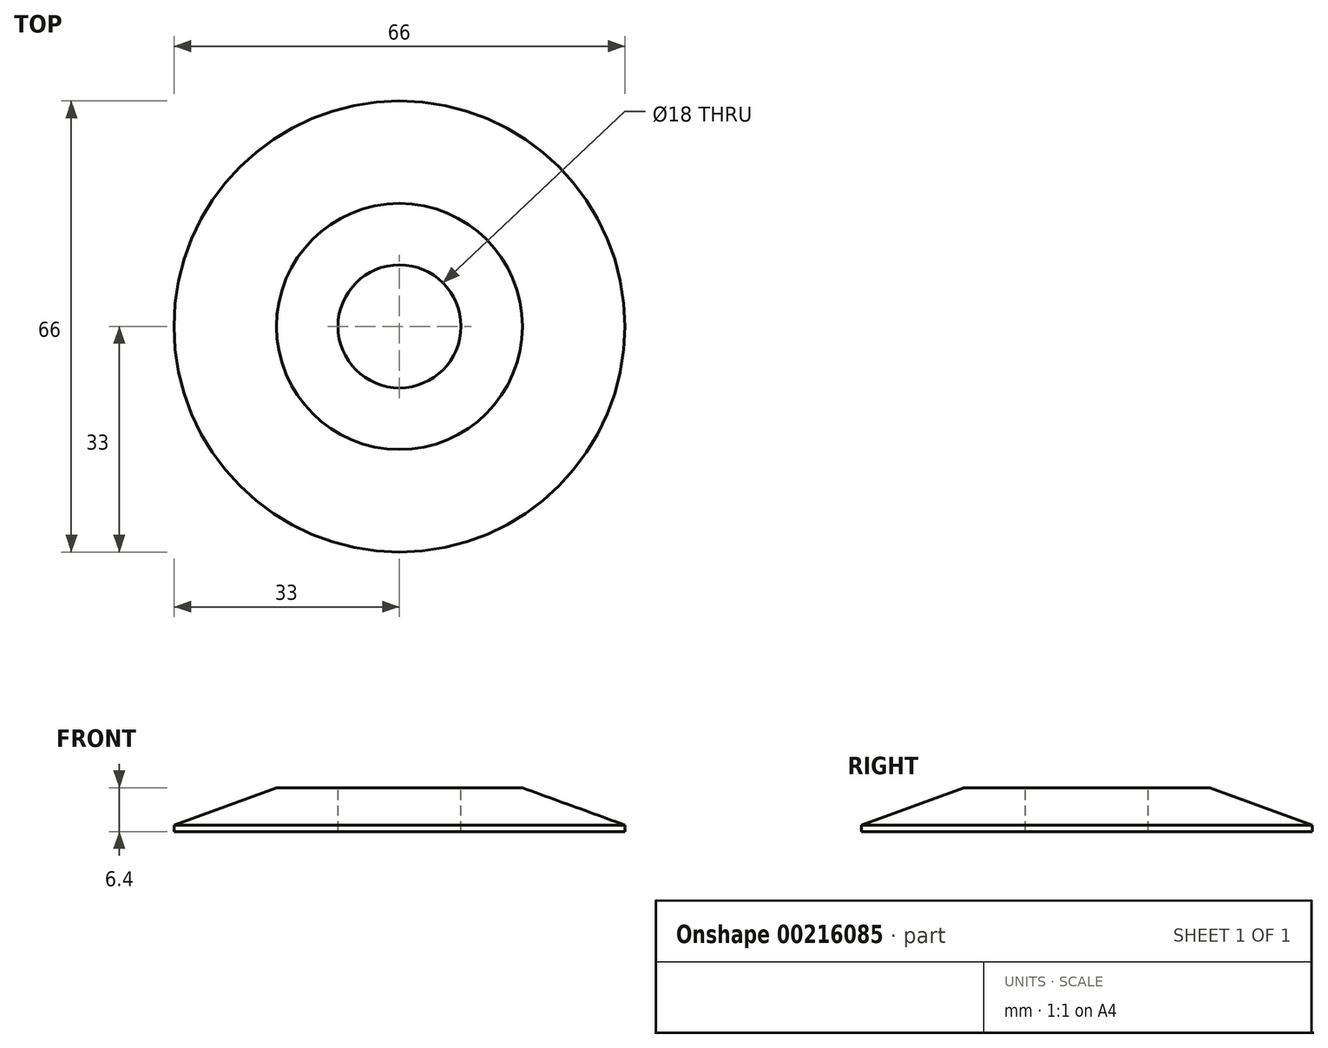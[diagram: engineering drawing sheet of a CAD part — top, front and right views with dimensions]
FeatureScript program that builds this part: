
annotation { "Feature Type Name" : "Feature", "Feature Type Description" : "" }
export const myFeature = defineFeature(function(context is Context, id is Id, definition is map)
    precondition{}
    {
        {
            var Q0;
            Q0=qCreatedBy(makeId("Top.planeOp"),FACE);
            var sketch = newSketch(context, id + "F0", { "sketchPlane" : qUnion([Q0])});
            skCircle(sketch, "E0", {"center": v(0, 0) * mm, "radius": 33 * mm});
            skSolve(sketch);
        }
        {
            var Q0;
            Q0 = qSketchRegion(id + "F0", true);
            extrude(context, id + "F1", {"entities" : qUnion([Q0]), "depth" : 6.4 * mm, "symmetric" : true});
        }
        {
            var Q0;
            Q0=makeQuery(id+"F1.opExtrude","CAP_FACE",FACE,{"disambiguationData":[OSD([sQuery(id+"F0.wireOp",EDGE,"E0")])],"isStart":false});
            var sketch = newSketch(context, id + "F2", { "sketchPlane" : qUnion([Q0])});
            skCircle(sketch, "E1", {"center": v(0, 0) * mm, "radius": 9 * mm});
            skSolve(sketch);
        }
        {
            var Q0;
            Q0=makeQuery(id+"F2.imprint","IMPRINT",FACE,{"disambiguationData":[TD([[makeQuery(id+"F2.imprint","IMPRINT",EDGE,{"derivedFrom":sQuery(id+"F2.wireOp",EDGE,"E1")}),1.0]])]});
            extrude(context, id + "F3", {"entities" : qUnion([Q0]), "operationType" : NewBodyOperationType.REMOVE, "endBound" : BoundingType.THROUGH_ALL, "oppositeDirection" : true, "depth" : 25 * mm});
        }
        {
            var Q0;
            Q0=makeQuery(id+"F1.opExtrude","CAP_EDGE",EDGE,{"disambiguationData":[OSD([sQuery(id+"F0.wireOp",EDGE,"E0")])],"isStart":false});
            chamfer(context, id + "F4", {"entities" : qUnion([Q0]), "chamferType" : ChamferType.OFFSET_ANGLE, "width" : 15 * mm, "oppositeDirection" : false, "angle" : 20 * degree, "tangentPropagation" : true});
        }
    });
